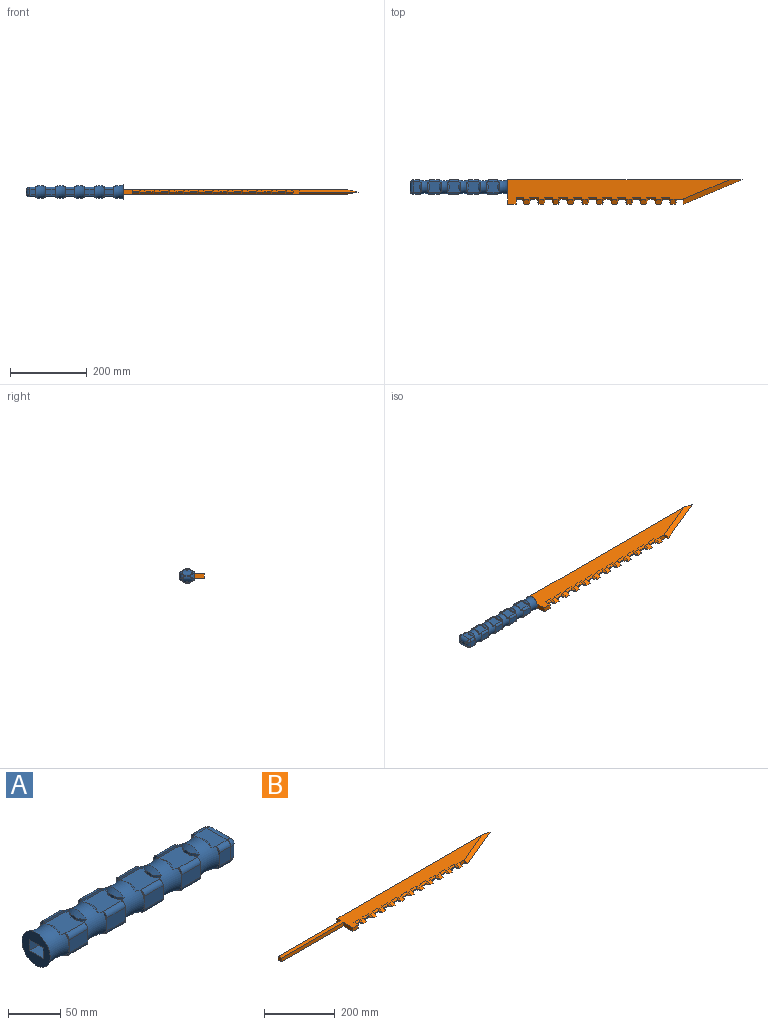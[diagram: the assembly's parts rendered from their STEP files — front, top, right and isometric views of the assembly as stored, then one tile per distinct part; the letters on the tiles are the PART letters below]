
ASSEMBLY  parts=2 mates=1
PART A: 212 faces, bbox 266.4x58.1x58.1 mm
  f0: plane 38.1x38.1mm, normal (-1,0,0), area 898.2mm2, adj f50,f207,f208,f209,f210
  f1: plane 12.69x4.85mm, normal (1,0,0), area 13.8mm2, adj f9,f71,f97
  f2: plane 12.69x4.85mm, normal (1,0,0), area 13.8mm2, adj f9,f71,f95
  f3: plane 12.69x4.85mm, normal (1,0,0), area 13.8mm2, adj f7,f71,f98
  f4: plane 12.69x4.85mm, normal (-1,0,0), area 13.8mm2, adj f9,f57,f97
  f5: plane 12.69x4.85mm, normal (-1,0,0), area 13.8mm2, adj f9,f57,f95
  f6: plane 12.69x4.85mm, normal (-1,0,0), area 13.8mm2, adj f7,f57,f98
  f7: plane 25.4x15.24mm, normal (0,-1,0), area 387.1mm2, adj f3,f6,f8,f10,f96,f98
  f8: plane 12.69x4.85mm, normal (1,0,0), area 13.8mm2, adj f7,f71,f96
  f9: plane 25.4x15.24mm, normal (0,1,0), area 387.1mm2, adj f1,f2,f4,f5,f95,f97
  f10: plane 12.69x4.85mm, normal (-1,0,0), area 13.8mm2, adj f7,f57,f96
  f11: plane 7.57x3.09mm, normal (1,0,0), area 22mm2, adj f75,f191,f192,f198
  f12: plane 12.69x4.85mm, normal (1,0,0), area 13.8mm2, adj f21,f57,f101
  f13: plane 12.69x4.85mm, normal (1,0,0), area 13.8mm2, adj f21,f57,f99
  f14: plane 12.69x4.85mm, normal (1,0,0), area 13.8mm2, adj f19,f57,f102
  f15: plane 12.69x4.85mm, normal (-1,0,0), area 13.8mm2, adj f21,f54,f101
  f16: plane 12.69x4.85mm, normal (-1,0,0), area 13.8mm2, adj f21,f54,f99
  f17: plane 12.69x4.85mm, normal (-1,0,0), area 13.8mm2, adj f19,f54,f102
  f18: plane 12.69x4.85mm, normal (-1,0,0), area 13.8mm2, adj f19,f54,f100
  f19: plane 25.4x15.24mm, normal (0,-1,0), area 387.1mm2, adj f14,f17,f18,f20,f100,f102
  f20: plane 12.69x4.85mm, normal (1,0,0), area 13.8mm2, adj f19,f57,f100
  f21: plane 25.4x15.24mm, normal (0,1,0), area 387.1mm2, adj f12,f13,f15,f16,f99,f101
  f22: plane 7.57x3.09mm, normal (1,0,0), area 22mm2, adj f77,f180,f181,f187
  f23: plane 12.69x4.85mm, normal (1,0,0), area 13.8mm2, adj f32,f54,f105
  f24: plane 12.69x4.85mm, normal (1,0,0), area 13.8mm2, adj f32,f54,f103
  f25: plane 12.69x4.85mm, normal (1,0,0), area 13.8mm2, adj f30,f54,f106
  f26: plane 12.69x4.85mm, normal (-1,0,0), area 13.8mm2, adj f32,f47,f105
  f27: plane 12.69x4.85mm, normal (-1,0,0), area 13.8mm2, adj f32,f47,f103
  f28: plane 12.69x4.85mm, normal (-1,0,0), area 13.8mm2, adj f30,f47,f106
  f29: plane 12.69x4.85mm, normal (-1,0,0), area 13.8mm2, adj f30,f47,f104
  f30: plane 25.4x15.24mm, normal (0,-1,0), area 387.1mm2, adj f25,f28,f29,f31,f104,f106
  f31: plane 12.69x4.85mm, normal (1,0,0), area 13.8mm2, adj f30,f54,f104
  f32: plane 25.4x15.24mm, normal (0,1,0), area 387.1mm2, adj f23,f24,f26,f27,f103,f105
  f33: plane 7.57x3.09mm, normal (1,0,0), area 22mm2, adj f79,f169,f170,f176
  f34: plane 12.69x4.85mm, normal (-1,0,0), area 13.8mm2, adj f40,f50,f109
  f35: plane 12.69x4.85mm, normal (-1,0,0), area 13.8mm2, adj f40,f50,f107
  f36: plane 12.69x4.85mm, normal (-1,0,0), area 13.8mm2, adj f42,f50,f110
  f37: plane 12.69x4.85mm, normal (1,0,0), area 13.8mm2, adj f40,f47,f109
  f38: plane 12.69x4.85mm, normal (1,0,0), area 13.8mm2, adj f40,f47,f107
  f39: plane 12.69x4.85mm, normal (1,0,0), area 13.8mm2, adj f42,f47,f110
  f40: plane 25.4x15.24mm, normal (0,1,0), area 387.1mm2, adj f34,f35,f37,f38,f107,f109
  f41: plane 12.69x4.85mm, normal (-1,0,0), area 13.8mm2, adj f42,f50,f108
  f42: plane 25.4x15.24mm, normal (0,-1,0), area 387.1mm2, adj f36,f39,f41,f43,f108,f110
  f43: plane 12.69x4.85mm, normal (1,0,0), area 13.8mm2, adj f42,f47,f108
  f44: plane 7.57x3.09mm, normal (-1,0,0), area 22mm2, adj f80,f163,f164,f165
  f45: plane 7.57x3.09mm, normal (-1,0,0), area 22mm2, adj f84,f114,f115,f121
  f46: plane 7.57x3.09mm, normal (1,0,0), area 22mm2, adj f83,f130,f131,f132
  f47: torus R=49.53mm, axis (-1,0,0), area 2213.5mm2, adj f26,f27,f28,f29,f37,f38,f39,f43
  f48: plane 7.57x3.09mm, normal (1,0,0), area 22mm2, adj f81,f158,f159,f165
  f49: plane 7.57x3.09mm, normal (1,0,0), area 22mm2, adj f82,f119,f120,f121
  f50: torus R=49.53mm, axis (-1,0,0), area 2528.7mm2, adj f0,f34,f35,f36,f41,f81,f82,f107
  f51: plane 7.57x3.09mm, normal (-1,0,0), area 22mm2, adj f78,f174,f175,f176
  f52: plane 7.57x3.09mm, normal (-1,0,0), area 22mm2, adj f85,f125,f126,f132
  f53: plane 7.57x3.09mm, normal (1,0,0), area 22mm2, adj f86,f141,f142,f143
  f54: torus R=49.53mm, axis (-1,0,0), area 2213.5mm2, adj f15,f16,f17,f18,f23,f24,f25,f31
  f55: plane 7.57x3.09mm, normal (-1,0,0), area 22mm2, adj f76,f185,f186,f187
  f56: plane 7.57x3.09mm, normal (1,0,0), area 22mm2, adj f88,f152,f153,f154
  f57: torus R=49.53mm, axis (-1,0,0), area 2213.5mm2, adj f4,f5,f6,f10,f12,f13,f14,f20
  f58: plane 7.57x3.09mm, normal (-1,0,0), area 22mm2, adj f87,f136,f137,f143
  f59: plane 7.57x3.09mm, normal (-1,0,0), area 22mm2, adj f74,f196,f197,f198
  f60: plane 12.69x4.85mm, normal (-1,0,0), area 13.8mm2, adj f66,f71,f94
  f61: plane 12.69x4.85mm, normal (-1,0,0), area 13.8mm2, adj f66,f71,f92
  f62: plane 12.69x4.85mm, normal (-1,0,0), area 13.8mm2, adj f64,f71,f93
  f63: plane 12.69x4.85mm, normal (-1,0,0), area 13.8mm2, adj f64,f71,f91
  f64: plane 15.24x15.24mm, normal (0,-1,0), area 232.3mm2, adj f62,f63,f91,f93,f206
  f65: plane 17.78x5.08mm, normal (1,0,0), area 90.3mm2, adj f199,f202,f203,f206
  f66: plane 15.24x15.24mm, normal (0,1,0), area 232.3mm2, adj f60,f61,f92,f94,f199
  f67: plane 29.57x22.05mm, normal (0,0,1), area 473.4mm2, adj f69,f71,f73,f93,f94,f202
  f68: plane 29.57x22.05mm, normal (0,0,-1), area 473.4mm2, adj f70,f71,f90,f91,f92,f203
  f69: plane 7.57x0.55mm, normal (1,0,0), area 2.8mm2, adj f67,f73
  f70: plane 7.57x0.55mm, normal (1,0,0), area 2.8mm2, adj f68,f90
  f71: torus R=49.53mm, axis (-1,0,0), area 2212.9mm2, adj f1,f2,f3,f8,f60,f61,f62,f63
  f72: plane 7.57x3.09mm, normal (-1,0,0), area 22mm2, adj f89,f147,f148,f154
  f73: cone r=17.37mm half-angle=38.4deg, axis (-1,0,0), area 107.8mm2, adj f67,f69,f71
  f74: cone r=13.25mm half-angle=38.4deg, axis (1,0,0), area 107.8mm2, adj f59,f71,f196,f197
  f75: cone r=17.37mm half-angle=38.4deg, axis (-1,0,0), area 107.8mm2, adj f11,f57,f191,f192
  f76: cone r=13.25mm half-angle=38.4deg, axis (1,0,0), area 107.8mm2, adj f55,f57,f185,f186
  f77: cone r=17.37mm half-angle=38.4deg, axis (-1,0,0), area 107.8mm2, adj f22,f54,f180,f181
  f78: cone r=13.25mm half-angle=38.4deg, axis (1,0,0), area 107.8mm2, adj f51,f54,f174,f175
  f79: cone r=17.37mm half-angle=38.4deg, axis (-1,0,0), area 107.8mm2, adj f33,f47,f169,f170
  f80: cone r=13.25mm half-angle=38.4deg, axis (1,0,0), area 107.8mm2, adj f44,f47,f163,f164
  f81: cone r=17.37mm half-angle=38.4deg, axis (-1,0,0), area 107.8mm2, adj f48,f50,f158,f159
  f82: cone r=17.37mm half-angle=38.4deg, axis (-1,0,0), area 107.8mm2, adj f49,f50,f119,f120
  f83: cone r=17.37mm half-angle=38.4deg, axis (-1,0,0), area 107.8mm2, adj f46,f47,f130,f131
  f84: cone r=13.25mm half-angle=38.4deg, axis (1,0,0), area 107.8mm2, adj f45,f47,f114,f115
  f85: cone r=13.25mm half-angle=38.4deg, axis (1,0,0), area 107.8mm2, adj f52,f54,f125,f126
  f86: cone r=17.37mm half-angle=38.4deg, axis (-1,0,0), area 107.8mm2, adj f53,f54,f141,f142
  f87: cone r=13.25mm half-angle=38.4deg, axis (1,0,0), area 107.8mm2, adj f57,f58,f136,f137
  f88: cone r=17.37mm half-angle=38.4deg, axis (-1,0,0), area 107.8mm2, adj f56,f57,f152,f153
  f89: cone r=13.25mm half-angle=38.4deg, axis (1,0,0), area 107.8mm2, adj f71,f72,f147,f148
  f90: cone r=17.37mm half-angle=38.4deg, axis (-1,0,0), area 107.8mm2, adj f68,f70,f71
  f91: cylinder r=5.08mm len=15.66mm, axis (1,0,0), area 121.7mm2, adj f63,f64,f68,f71,f205
  f92: cylinder r=5.08mm len=15.66mm, axis (-1,0,0), area 121.7mm2, adj f61,f66,f68,f71,f201
  f93: cylinder r=5.08mm len=15.66mm, axis (-1,0,0), area 121.7mm2, adj f62,f64,f67,f71,f204
  f94: cylinder r=5.08mm len=15.66mm, axis (1,0,0), area 121.7mm2, adj f60,f66,f67,f71,f200
  f95: cylinder r=5.08mm len=26.23mm, axis (-1,0,0), area 202.8mm2, adj f2,f5,f9,f57,f71,f145
  f96: cylinder r=5.08mm len=26.23mm, axis (1,0,0), area 202.8mm2, adj f7,f8,f10,f57,f71,f150
  f97: cylinder r=5.08mm len=26.23mm, axis (1,0,0), area 202.8mm2, adj f1,f4,f9,f57,f71,f189
  f98: cylinder r=5.08mm len=26.23mm, axis (-1,0,0), area 202.8mm2, adj f3,f6,f7,f57,f71,f194
  f99: cylinder r=5.08mm len=26.23mm, axis (-1,0,0), area 202.8mm2, adj f13,f16,f21,f54,f57,f134
  f100: cylinder r=5.08mm len=26.23mm, axis (1,0,0), area 202.8mm2, adj f18,f19,f20,f54,f57,f139
  f101: cylinder r=5.08mm len=26.23mm, axis (1,0,0), area 202.8mm2, adj f12,f15,f21,f54,f57,f178
  f102: cylinder r=5.08mm len=26.23mm, axis (-1,0,0), area 202.8mm2, adj f14,f17,f19,f54,f57,f183
  f103: cylinder r=5.08mm len=26.23mm, axis (-1,0,0), area 202.8mm2, adj f24,f27,f32,f47,f54,f123
  f104: cylinder r=5.08mm len=26.23mm, axis (1,0,0), area 202.8mm2, adj f29,f30,f31,f47,f54,f128
  f105: cylinder r=5.08mm len=26.23mm, axis (1,0,0), area 202.8mm2, adj f23,f26,f32,f47,f54,f167
  f106: cylinder r=5.08mm len=26.23mm, axis (-1,0,0), area 202.8mm2, adj f25,f28,f30,f47,f54,f172
  f107: cylinder r=5.08mm len=26.23mm, axis (-1,0,0), area 202.8mm2, adj f35,f38,f40,f47,f50,f112
  f108: cylinder r=5.08mm len=26.23mm, axis (1,0,0), area 202.8mm2, adj f41,f42,f43,f47,f50,f117
  f109: cylinder r=5.08mm len=26.23mm, axis (1,0,0), area 202.8mm2, adj f34,f37,f40,f47,f50,f156
  f110: cylinder r=5.08mm len=26.23mm, axis (-1,0,0), area 202.8mm2, adj f36,f39,f42,f47,f50,f161
  f111: extruded ~4.78x2.54mm, area 13.3mm2, adj f50,f112,f120,f121
  f112: plane 26.23x2.54mm, normal (0,-1,0), area 66.6mm2, adj f107,f111,f113,f121
  f113: extruded ~4.78x2.54mm, area 13.3mm2, adj f47,f112,f114,f121
  f114: extruded ~8.07x5.2mm, area 24.5mm2, adj f45,f84,f113,f121
  f115: extruded ~8.07x5.2mm, area 24.5mm2, adj f45,f84,f116,f121
  f116: extruded ~4.78x2.54mm, area 13.3mm2, adj f47,f115,f117,f121
  f117: plane 26.23x2.54mm, normal (0,1,0), area 66.6mm2, adj f108,f116,f118,f121
  f118: extruded ~4.78x2.54mm, area 13.3mm2, adj f50,f117,f119,f121
  f119: extruded ~8.07x5.2mm, area 24.5mm2, adj f49,f82,f118,f121
  f120: extruded ~8.07x5.2mm, area 24.5mm2, adj f49,f82,f111,f121
  f121: plane 36.06x28.21mm, normal (0,0,-1), area 805.1mm2, adj f45,f49,f111,f112,f113,f114,f115,f116
  f122: extruded ~4.78x2.54mm, area 13.3mm2, adj f47,f123,f131,f132
  f123: plane 26.23x2.54mm, normal (0,-1,0), area 66.6mm2, adj f103,f122,f124,f132
  f124: extruded ~4.78x2.54mm, area 13.3mm2, adj f54,f123,f125,f132
  f125: extruded ~8.07x5.2mm, area 24.5mm2, adj f52,f85,f124,f132
  f126: extruded ~8.07x5.2mm, area 24.5mm2, adj f52,f85,f127,f132
  f127: extruded ~4.78x2.54mm, area 13.3mm2, adj f54,f126,f128,f132
  f128: plane 26.23x2.54mm, normal (0,1,0), area 66.6mm2, adj f104,f127,f129,f132
  f129: extruded ~4.78x2.54mm, area 13.3mm2, adj f47,f128,f130,f132
  f130: extruded ~8.07x5.2mm, area 24.5mm2, adj f46,f83,f129,f132
  f131: extruded ~8.07x5.2mm, area 24.5mm2, adj f46,f83,f122,f132
  f132: plane 36.06x28.21mm, normal (0,0,-1), area 805.1mm2, adj f46,f52,f122,f123,f124,f125,f126,f127
  f133: extruded ~4.78x2.54mm, area 13.3mm2, adj f54,f134,f142,f143
  f134: plane 26.23x2.54mm, normal (0,-1,0), area 66.6mm2, adj f99,f133,f135,f143
  f135: extruded ~4.78x2.54mm, area 13.3mm2, adj f57,f134,f136,f143
  f136: extruded ~8.07x5.2mm, area 24.5mm2, adj f58,f87,f135,f143
  f137: extruded ~8.07x5.2mm, area 24.5mm2, adj f58,f87,f138,f143
  f138: extruded ~4.78x2.54mm, area 13.3mm2, adj f57,f137,f139,f143
  f139: plane 26.23x2.54mm, normal (0,1,0), area 66.6mm2, adj f100,f138,f140,f143
  f140: extruded ~4.78x2.54mm, area 13.3mm2, adj f54,f139,f141,f143
  f141: extruded ~8.07x5.2mm, area 24.5mm2, adj f53,f86,f140,f143
  f142: extruded ~8.07x5.2mm, area 24.5mm2, adj f53,f86,f133,f143
  f143: plane 36.06x28.21mm, normal (0,0,-1), area 805.1mm2, adj f53,f58,f133,f134,f135,f136,f137,f138
  f144: extruded ~4.78x2.54mm, area 13.3mm2, adj f57,f145,f153,f154
  f145: plane 26.23x2.54mm, normal (0,-1,0), area 66.6mm2, adj f95,f144,f146,f154
  f146: extruded ~4.78x2.54mm, area 13.3mm2, adj f71,f145,f147,f154
  f147: extruded ~8.07x5.2mm, area 24.5mm2, adj f72,f89,f146,f154
  f148: extruded ~8.07x5.2mm, area 24.5mm2, adj f72,f89,f149,f154
  f149: extruded ~4.78x2.54mm, area 13.3mm2, adj f71,f148,f150,f154
  f150: plane 26.23x2.54mm, normal (0,1,0), area 66.6mm2, adj f96,f149,f151,f154
  f151: extruded ~4.78x2.54mm, area 13.3mm2, adj f57,f150,f152,f154
  f152: extruded ~8.07x5.2mm, area 24.5mm2, adj f56,f88,f151,f154
  f153: extruded ~8.07x5.2mm, area 24.5mm2, adj f56,f88,f144,f154
  f154: plane 36.06x28.21mm, normal (0,0,-1), area 805.1mm2, adj f56,f72,f144,f145,f146,f147,f148,f149
  f155: extruded ~4.78x2.54mm, area 13.3mm2, adj f47,f156,f164,f165
  f156: plane 26.23x2.54mm, normal (0,-1,0), area 66.6mm2, adj f109,f155,f157,f165
  f157: extruded ~4.78x2.54mm, area 13.3mm2, adj f50,f156,f158,f165
  f158: extruded ~8.07x5.2mm, area 24.5mm2, adj f48,f81,f157,f165
  f159: extruded ~8.07x5.2mm, area 24.5mm2, adj f48,f81,f160,f165
  f160: extruded ~4.78x2.54mm, area 13.3mm2, adj f50,f159,f161,f165
  f161: plane 26.23x2.54mm, normal (0,1,0), area 66.6mm2, adj f110,f160,f162,f165
  f162: extruded ~4.78x2.54mm, area 13.3mm2, adj f47,f161,f163,f165
  f163: extruded ~8.07x5.2mm, area 24.5mm2, adj f44,f80,f162,f165
  f164: extruded ~8.07x5.2mm, area 24.5mm2, adj f44,f80,f155,f165
  f165: plane 35.79x27.94mm, normal (0,0,1), area 804.9mm2, adj f44,f48,f155,f156,f157,f158,f159,f160
  f166: extruded ~4.78x2.54mm, area 13.3mm2, adj f54,f167,f175,f176
  f167: plane 26.23x2.54mm, normal (0,-1,0), area 66.6mm2, adj f105,f166,f168,f176
  f168: extruded ~4.78x2.54mm, area 13.3mm2, adj f47,f167,f169,f176
  f169: extruded ~8.07x5.2mm, area 24.5mm2, adj f33,f79,f168,f176
  f170: extruded ~8.07x5.2mm, area 24.5mm2, adj f33,f79,f171,f176
  f171: extruded ~4.78x2.54mm, area 13.3mm2, adj f47,f170,f172,f176
  f172: plane 26.23x2.54mm, normal (0,1,0), area 66.6mm2, adj f106,f171,f173,f176
  f173: extruded ~4.78x2.54mm, area 13.3mm2, adj f54,f172,f174,f176
  f174: extruded ~8.07x5.2mm, area 24.5mm2, adj f51,f78,f173,f176
  f175: extruded ~8.07x5.2mm, area 24.5mm2, adj f51,f78,f166,f176
  f176: plane 35.79x27.94mm, normal (0,0,1), area 804.9mm2, adj f33,f51,f166,f167,f168,f169,f170,f171
  f177: extruded ~4.78x2.54mm, area 13.3mm2, adj f57,f178,f186,f187
  f178: plane 26.23x2.54mm, normal (0,-1,0), area 66.6mm2, adj f101,f177,f179,f187
  f179: extruded ~4.78x2.54mm, area 13.3mm2, adj f54,f178,f180,f187
  f180: extruded ~8.07x5.2mm, area 24.5mm2, adj f22,f77,f179,f187
  f181: extruded ~8.07x5.2mm, area 24.5mm2, adj f22,f77,f182,f187
  f182: extruded ~4.78x2.54mm, area 13.3mm2, adj f54,f181,f183,f187
  f183: plane 26.23x2.54mm, normal (0,1,0), area 66.6mm2, adj f102,f182,f184,f187
  f184: extruded ~4.78x2.54mm, area 13.3mm2, adj f57,f183,f185,f187
  f185: extruded ~8.07x5.2mm, area 24.5mm2, adj f55,f76,f184,f187
  f186: extruded ~8.07x5.2mm, area 24.5mm2, adj f55,f76,f177,f187
  f187: plane 35.79x27.94mm, normal (0,0,1), area 804.9mm2, adj f22,f55,f177,f178,f179,f180,f181,f182
  f188: extruded ~4.78x2.54mm, area 13.3mm2, adj f71,f189,f197,f198
  f189: plane 26.23x2.54mm, normal (0,-1,0), area 66.6mm2, adj f97,f188,f190,f198
  f190: extruded ~4.78x2.54mm, area 13.3mm2, adj f57,f189,f191,f198
  f191: extruded ~8.07x5.2mm, area 24.5mm2, adj f11,f75,f190,f198
  f192: extruded ~8.07x5.2mm, area 24.5mm2, adj f11,f75,f193,f198
  f193: extruded ~4.78x2.54mm, area 13.3mm2, adj f57,f192,f194,f198
  f194: plane 26.23x2.54mm, normal (0,1,0), area 66.6mm2, adj f98,f193,f195,f198
  f195: extruded ~4.78x2.54mm, area 13.3mm2, adj f71,f194,f196,f198
  f196: extruded ~8.07x5.2mm, area 24.5mm2, adj f59,f74,f195,f198
  f197: extruded ~8.07x5.2mm, area 24.5mm2, adj f59,f74,f188,f198
  f198: plane 35.79x27.94mm, normal (0,0,1), area 804.9mm2, adj f11,f59,f188,f189,f190,f191,f192,f193
  f199: cylinder r=10.16mm len=15.24mm, axis (0,0,-1), area 162.1mm2, adj f65,f66,f200,f201
  f200: bspline ~12.13x10.16mm, area 56.1mm2, adj f94,f199,f202
  f201: bspline ~12.13x10.16mm, area 56.1mm2, adj f92,f199,f203
  f202: cylinder r=10.16mm len=27.94mm, axis (0,-1,0), area 364.8mm2, adj f65,f67,f200,f204
  f203: cylinder r=10.16mm len=27.94mm, axis (0,1,0), area 364.8mm2, adj f65,f68,f201,f205
  f204: bspline ~12.13x10.16mm, area 56.1mm2, adj f93,f202,f206
  f205: bspline ~12.13x10.16mm, area 85.2mm2, adj f91,f203,f206
  f206: cylinder r=10.16mm len=15.24mm, axis (0,0,1), area 162.1mm2, adj f64,f65,f204,f205
  f207: plane 247.65x12.7mm, normal (0,1,0), area 3145.2mm2, adj f0,f208,f210,f211
  f208: plane 247.65x19.05mm, normal (0,0,-1), area 4717.7mm2, adj f0,f207,f209,f211
  f209: plane 247.65x12.7mm, normal (0,-1,0), area 3145.2mm2, adj f0,f208,f210,f211
  f210: plane 247.65x19.05mm, normal (0,0,1), area 4717.7mm2, adj f0,f207,f209,f211
  f211: plane 19.05x12.7mm, normal (-1,0,0), area 241.9mm2, adj f207,f208,f209,f210
PART B: 135 faces, bbox 857.3x63.5x12.7 mm
  f0: plane 1.34x1.34mm, normal (-1,0,0), area 0.9mm2, adj f35,f110,f111
  f1: plane 1.34x1.34mm, normal (1,0,0), area 0.9mm2, adj f2,f88,f89
  f2: plane 17.18x2.54mm, normal (0,-1,0), area 41.5mm2, adj f1,f3,f76,f77,f88,f89,f108,f109
  f3: plane 1.34x1.34mm, normal (-1,0,0), area 0.9mm2, adj f2,f108,f109
  f4: plane 1.34x1.34mm, normal (1,0,0), area 0.9mm2, adj f5,f86,f87
  f5: plane 17.18x2.54mm, normal (0,-1,0), area 41.5mm2, adj f4,f6,f78,f79,f86,f87,f106,f107
  f6: plane 1.34x1.34mm, normal (-1,0,0), area 0.9mm2, adj f5,f106,f107
  f7: plane 1.34x1.34mm, normal (1,0,0), area 0.9mm2, adj f8,f84,f85
  f8: plane 21.18x12.7mm, normal (0,-1,0), area 232.1mm2, adj f7,f9,f36,f37,f38,f60,f84,f85
  f9: plane 12.7x11.72mm, normal (-1,0,0), area 74.4mm2, adj f8,f38,f60
  f10: plane 609.6x12.7mm, normal (0,1,0), area 7532.2mm2, adj f36,f37,f38,f60,f134
  f11: plane 16.64x2.54mm, normal (0,-1,0), area 41.2mm2, adj f12,f82,f83,f126,f127,f133
  f12: plane 1.34x1.34mm, normal (-1,0,0), area 0.9mm2, adj f11,f126,f127
  f13: plane 1.34x1.34mm, normal (1,0,0), area 0.9mm2, adj f14,f124,f125
  f14: plane 17.18x2.54mm, normal (0,-1,0), area 41.5mm2, adj f13,f15,f80,f81,f122,f123,f124,f125
  f15: plane 1.34x1.34mm, normal (-1,0,0), area 0.9mm2, adj f14,f122,f123
  f16: plane 1.34x1.34mm, normal (1,0,0), area 0.9mm2, adj f17,f104,f105
  f17: plane 17.18x2.54mm, normal (0,-1,0), area 41.5mm2, adj f16,f18,f62,f63,f104,f105,f120,f121
  f18: plane 1.34x1.34mm, normal (-1,0,0), area 0.9mm2, adj f17,f120,f121
  f19: plane 1.34x1.34mm, normal (1,0,0), area 0.9mm2, adj f20,f102,f103
  f20: plane 17.18x2.54mm, normal (0,-1,0), area 41.5mm2, adj f19,f21,f64,f65,f102,f103,f118,f119
  f21: plane 1.34x1.34mm, normal (-1,0,0), area 0.9mm2, adj f20,f118,f119
  f22: plane 1.34x1.34mm, normal (1,0,0), area 0.9mm2, adj f23,f100,f101
  f23: plane 17.18x2.54mm, normal (0,-1,0), area 41.5mm2, adj f22,f24,f66,f67,f100,f101,f116,f117
  f24: plane 1.34x1.34mm, normal (-1,0,0), area 0.9mm2, adj f23,f116,f117
  f25: plane 1.34x1.34mm, normal (1,0,0), area 0.9mm2, adj f26,f98,f99
  f26: plane 17.18x2.54mm, normal (0,-1,0), area 41.5mm2, adj f25,f27,f68,f69,f98,f99,f114,f115
  f27: plane 1.34x1.34mm, normal (-1,0,0), area 0.9mm2, adj f26,f114,f115
  f28: plane 1.34x1.34mm, normal (1,0,0), area 0.9mm2, adj f29,f96,f97
  f29: plane 17.18x2.54mm, normal (0,-1,0), area 41.5mm2, adj f28,f30,f70,f71,f94,f95,f96,f97
  f30: plane 1.34x1.34mm, normal (-1,0,0), area 0.9mm2, adj f29,f94,f95
  f31: plane 1.34x1.34mm, normal (1,0,0), area 0.9mm2, adj f32,f92,f93
  f32: plane 17.18x2.54mm, normal (0,-1,0), area 41.5mm2, adj f31,f33,f72,f73,f92,f93,f112,f113
  f33: plane 1.34x1.34mm, normal (-1,0,0), area 0.9mm2, adj f32,f112,f113
  f34: plane 1.34x1.34mm, normal (1,0,0), area 0.9mm2, adj f35,f90,f91
  f35: plane 17.18x2.54mm, normal (0,-1,0), area 41.5mm2, adj f0,f34,f74,f75,f90,f91,f110,f111
  f36: plane 824.23x63.5mm, normal (0,0,1), area 28297.4mm2, adj f8,f10,f38,f39,f40,f41,f42,f43
  f37: plane 824.23x63.5mm, normal (0,0,-1), area 28297.4mm2, adj f8,f10,f50,f51,f52,f53,f54,f55
  f38: plane 154.94x63.5mm, normal (0.17,-0.41,0.89), area 2091.8mm2, adj f8,f9,f10,f36,f60
  f39: plane 12.7x11.84mm, normal (0,-0.45,0.89), area 168.1mm2, adj f36,f57,f88,f111
  f40: plane 12.7x11.84mm, normal (0,-0.45,0.89), area 168.1mm2, adj f36,f58,f87,f109
  f41: plane 12.7x11.84mm, normal (0,-0.45,0.89), area 168.1mm2, adj f36,f59,f84,f107
  f42: plane 12.7x11.84mm, normal (0,-0.45,0.89), area 168.1mm2, adj f36,f56,f90,f113
  f43: plane 12.7x11.84mm, normal (0,-0.45,0.89), area 168.1mm2, adj f36,f55,f93,f95
  f44: plane 12.7x11.84mm, normal (0,-0.45,0.89), area 168.1mm2, adj f36,f54,f96,f115
  f45: plane 12.7x11.84mm, normal (0,-0.45,0.89), area 168.1mm2, adj f36,f53,f98,f116
  f46: plane 12.7x11.84mm, normal (0,-0.45,0.89), area 168.1mm2, adj f36,f52,f100,f119
  f47: plane 12.7x11.84mm, normal (0,-0.45,0.89), area 168.1mm2, adj f36,f51,f102,f121
  f48: plane 12.7x11.84mm, normal (0,-0.45,0.89), area 168.1mm2, adj f36,f50,f104,f123
  f49: plane 12.7x11.84mm, normal (0,-0.45,0.89), area 168.1mm2, adj f36,f61,f125,f127
  f50: plane 12.7x11.84mm, normal (0,-0.45,-0.89), area 168.1mm2, adj f37,f48,f105,f122
  f51: plane 12.7x11.84mm, normal (0,-0.45,-0.89), area 168.1mm2, adj f37,f47,f103,f120
  f52: plane 12.7x11.84mm, normal (0,-0.45,-0.89), area 168.1mm2, adj f37,f46,f101,f118
  f53: plane 12.7x11.84mm, normal (0,-0.45,-0.89), area 168.1mm2, adj f37,f45,f99,f117
  f54: plane 12.7x11.84mm, normal (0,-0.45,-0.89), area 168.1mm2, adj f37,f44,f97,f114
  f55: plane 12.7x11.84mm, normal (0,-0.45,-0.89), area 168.1mm2, adj f37,f43,f92,f94
  f56: plane 12.7x11.84mm, normal (0,-0.45,-0.89), area 168.1mm2, adj f37,f42,f91,f112
  f57: plane 12.7x11.84mm, normal (0,-0.45,-0.89), area 168.1mm2, adj f37,f39,f89,f110
  f58: plane 12.7x11.84mm, normal (0,-0.45,-0.89), area 168.1mm2, adj f37,f40,f86,f108
  f59: plane 12.7x11.84mm, normal (0,-0.45,-0.89), area 168.1mm2, adj f37,f41,f85,f106
  f60: plane 154.94x63.5mm, normal (0.17,-0.41,-0.89), area 2091.8mm2, adj f8,f9,f10,f37,f38
  f61: plane 12.7x11.84mm, normal (0,-0.45,-0.89), area 168.1mm2, adj f37,f49,f124,f126
  f62: plane 21.72x5.08mm, normal (0,-0.71,-0.71), area 139.7mm2, adj f17,f37,f105,f120
  f63: plane 21.72x5.08mm, normal (0,-0.71,0.71), area 139.7mm2, adj f17,f36,f104,f121
  f64: plane 21.72x5.08mm, normal (0,-0.71,-0.71), area 139.7mm2, adj f20,f37,f103,f118
  f65: plane 21.72x5.08mm, normal (0,-0.71,0.71), area 139.7mm2, adj f20,f36,f102,f119
  f66: plane 21.72x5.08mm, normal (0,-0.71,-0.71), area 139.7mm2, adj f23,f37,f101,f117
  f67: plane 21.72x5.08mm, normal (0,-0.71,0.71), area 139.7mm2, adj f23,f36,f100,f116
  f68: plane 21.72x5.08mm, normal (0,-0.71,-0.71), area 139.7mm2, adj f26,f37,f99,f114
  f69: plane 21.72x5.08mm, normal (0,-0.71,0.71), area 139.7mm2, adj f26,f36,f98,f115
  f70: plane 21.72x5.08mm, normal (0,-0.71,-0.71), area 139.7mm2, adj f29,f37,f94,f97
  f71: plane 21.72x5.08mm, normal (0,-0.71,0.71), area 139.7mm2, adj f29,f36,f95,f96
  f72: plane 21.72x5.08mm, normal (0,-0.71,-0.71), area 139.7mm2, adj f32,f37,f92,f112
  f73: plane 21.72x5.08mm, normal (0,-0.71,0.71), area 139.7mm2, adj f32,f36,f93,f113
  f74: plane 21.72x5.08mm, normal (0,-0.71,-0.71), area 139.7mm2, adj f35,f37,f91,f110
  f75: plane 21.72x5.08mm, normal (0,-0.71,0.71), area 139.7mm2, adj f35,f36,f90,f111
  f76: plane 21.72x5.08mm, normal (0,-0.71,-0.71), area 139.7mm2, adj f2,f37,f89,f108
  f77: plane 21.72x5.08mm, normal (0,-0.71,0.71), area 139.7mm2, adj f2,f36,f88,f109
  f78: plane 21.72x5.08mm, normal (0,-0.71,-0.71), area 139.7mm2, adj f5,f37,f86,f106
  f79: plane 21.72x5.08mm, normal (0,-0.71,0.71), area 139.7mm2, adj f5,f36,f87,f107
  f80: plane 21.72x5.08mm, normal (0,-0.71,-0.71), area 139.7mm2, adj f14,f37,f122,f124
  f81: plane 21.72x5.08mm, normal (0,-0.71,0.71), area 139.7mm2, adj f14,f36,f123,f125
  f82: plane 18.91x5.08mm, normal (0,-0.71,-0.71), area 127.7mm2, adj f11,f37,f126,f133
  f83: plane 18.91x5.08mm, normal (0,-0.71,0.71), area 127.7mm2, adj f11,f36,f127,f133
  f84: plane 12.7x6.35mm, normal (0.71,-0.32,0.63), area 56.4mm2, adj f7,f8,f41,f85
  f85: plane 12.7x6.35mm, normal (0.71,-0.32,-0.63), area 56.4mm2, adj f7,f8,f59,f84
  f86: plane 17.78x6.35mm, normal (0.71,-0.32,-0.63), area 74.6mm2, adj f4,f5,f37,f58,f78,f87
  f87: plane 17.78x6.35mm, normal (0.71,-0.32,0.63), area 74.6mm2, adj f4,f5,f36,f40,f79,f86
  f88: plane 17.78x6.35mm, normal (0.71,-0.32,0.63), area 74.6mm2, adj f1,f2,f36,f39,f77,f89
  f89: plane 17.78x6.35mm, normal (0.71,-0.32,-0.63), area 74.6mm2, adj f1,f2,f37,f57,f76,f88
  f90: plane 17.78x6.35mm, normal (0.71,-0.32,0.63), area 74.6mm2, adj f34,f35,f36,f42,f75,f91
  f91: plane 17.78x6.35mm, normal (0.71,-0.32,-0.63), area 74.6mm2, adj f34,f35,f37,f56,f74,f90
  f92: plane 17.78x6.35mm, normal (0.71,-0.32,-0.63), area 74.6mm2, adj f31,f32,f37,f55,f72,f93
  f93: plane 17.78x6.35mm, normal (0.71,-0.32,0.63), area 74.6mm2, adj f31,f32,f36,f43,f73,f92
  f94: plane 17.78x6.35mm, normal (-0.71,-0.32,-0.63), area 74.6mm2, adj f29,f30,f37,f55,f70,f95
  f95: plane 17.78x6.35mm, normal (-0.71,-0.32,0.63), area 74.6mm2, adj f29,f30,f36,f43,f71,f94
  f96: plane 17.78x6.35mm, normal (0.71,-0.32,0.63), area 74.6mm2, adj f28,f29,f36,f44,f71,f97
  f97: plane 17.78x6.35mm, normal (0.71,-0.32,-0.63), area 74.6mm2, adj f28,f29,f37,f54,f70,f96
  f98: plane 17.78x6.35mm, normal (0.71,-0.32,0.63), area 74.6mm2, adj f25,f26,f36,f45,f69,f99
  f99: plane 17.78x6.35mm, normal (0.71,-0.32,-0.63), area 74.6mm2, adj f25,f26,f37,f53,f68,f98
  f100: plane 17.78x6.35mm, normal (0.71,-0.32,0.63), area 74.6mm2, adj f22,f23,f36,f46,f67,f101
  f101: plane 17.78x6.35mm, normal (0.71,-0.32,-0.63), area 74.6mm2, adj f22,f23,f37,f52,f66,f100
  f102: plane 17.78x6.35mm, normal (0.71,-0.32,0.63), area 74.6mm2, adj f19,f20,f36,f47,f65,f103
  f103: plane 17.78x6.35mm, normal (0.71,-0.32,-0.63), area 74.6mm2, adj f19,f20,f37,f51,f64,f102
  f104: plane 17.78x6.35mm, normal (0.71,-0.32,0.63), area 74.6mm2, adj f16,f17,f36,f48,f63,f105
  f105: plane 17.78x6.35mm, normal (0.71,-0.32,-0.63), area 74.6mm2, adj f16,f17,f37,f50,f62,f104
  f106: plane 17.78x6.35mm, normal (-0.71,-0.32,-0.63), area 74.6mm2, adj f5,f6,f37,f59,f78,f107
  f107: plane 17.78x6.35mm, normal (-0.71,-0.32,0.63), area 74.6mm2, adj f5,f6,f36,f41,f79,f106
  f108: plane 17.78x6.35mm, normal (-0.71,-0.32,-0.63), area 74.6mm2, adj f2,f3,f37,f58,f76,f109
  f109: plane 17.78x6.35mm, normal (-0.71,-0.32,0.63), area 74.6mm2, adj f2,f3,f36,f40,f77,f108
  f110: plane 17.78x6.35mm, normal (-0.71,-0.32,-0.63), area 74.6mm2, adj f0,f35,f37,f57,f74,f111
  f111: plane 17.78x6.35mm, normal (-0.71,-0.32,0.63), area 74.6mm2, adj f0,f35,f36,f39,f75,f110
  f112: plane 17.78x6.35mm, normal (-0.71,-0.32,-0.63), area 74.6mm2, adj f32,f33,f37,f56,f72,f113
  f113: plane 17.78x6.35mm, normal (-0.71,-0.32,0.63), area 74.6mm2, adj f32,f33,f36,f42,f73,f112
  f114: plane 17.78x6.35mm, normal (-0.71,-0.32,-0.63), area 74.6mm2, adj f26,f27,f37,f54,f68,f115
  f115: plane 17.78x6.35mm, normal (-0.71,-0.32,0.63), area 74.6mm2, adj f26,f27,f36,f44,f69,f114
  f116: plane 17.78x6.35mm, normal (-0.71,-0.32,0.63), area 74.6mm2, adj f23,f24,f36,f45,f67,f117
  f117: plane 17.78x6.35mm, normal (-0.71,-0.32,-0.63), area 74.6mm2, adj f23,f24,f37,f53,f66,f116
  f118: plane 17.78x6.35mm, normal (-0.71,-0.32,-0.63), area 74.6mm2, adj f20,f21,f37,f52,f64,f119
  f119: plane 17.78x6.35mm, normal (-0.71,-0.32,0.63), area 74.6mm2, adj f20,f21,f36,f46,f65,f118
  f120: plane 17.78x6.35mm, normal (-0.71,-0.32,-0.63), area 74.6mm2, adj f17,f18,f37,f51,f62,f121
  f121: plane 17.78x6.35mm, normal (-0.71,-0.32,0.63), area 74.6mm2, adj f17,f18,f36,f47,f63,f120
  f122: plane 17.78x6.35mm, normal (-0.71,-0.32,-0.63), area 74.6mm2, adj f14,f15,f37,f50,f80,f123
  f123: plane 17.78x6.35mm, normal (-0.71,-0.32,0.63), area 74.6mm2, adj f14,f15,f36,f48,f81,f122
  f124: plane 17.78x6.35mm, normal (0.71,-0.32,-0.63), area 74.6mm2, adj f13,f14,f37,f61,f80,f125
  f125: plane 17.78x6.35mm, normal (0.71,-0.32,0.63), area 74.6mm2, adj f13,f14,f36,f49,f81,f124
  f126: plane 17.78x6.35mm, normal (-0.71,-0.32,-0.63), area 74.6mm2, adj f11,f12,f37,f61,f82,f127
  f127: plane 17.78x6.35mm, normal (-0.71,-0.32,0.63), area 74.6mm2, adj f11,f12,f36,f49,f83,f126
  f128: plane 247.65x12.7mm, normal (0,1,0), area 3145.2mm2, adj f36,f37,f129,f134
  f129: plane 12.7x12.7mm, normal (-1,0,0), area 161.3mm2, adj f36,f37,f128,f130
  f130: plane 247.65x12.7mm, normal (0,-1,0), area 3145.2mm2, adj f36,f37,f129,f131
  f131: plane 38.1x12.7mm, normal (-1,0,0), area 483.9mm2, adj f36,f37,f130,f132
  f132: plane 22x12.7mm, normal (0,-1,0), area 279.4mm2, adj f36,f37,f131,f133
  f133: plane 17.78x12.7mm, normal (1,0,0), area 187.1mm2, adj f11,f36,f37,f82,f83,f132
  f134: plane 12.7x12.7mm, normal (-1,0,0), area 161.3mm2, adj f10,f36,f37,f128
PLACE A rot(axis=(0,0,1),180deg) t=(100.28,227.4,-35.31)mm
PLACE B t=(106.58,156.13,-41.66)mm
MATE fastened A.f50 <-> B.f129  axis (1,0,0) through (-21.2,195.06,-35.31)mm
